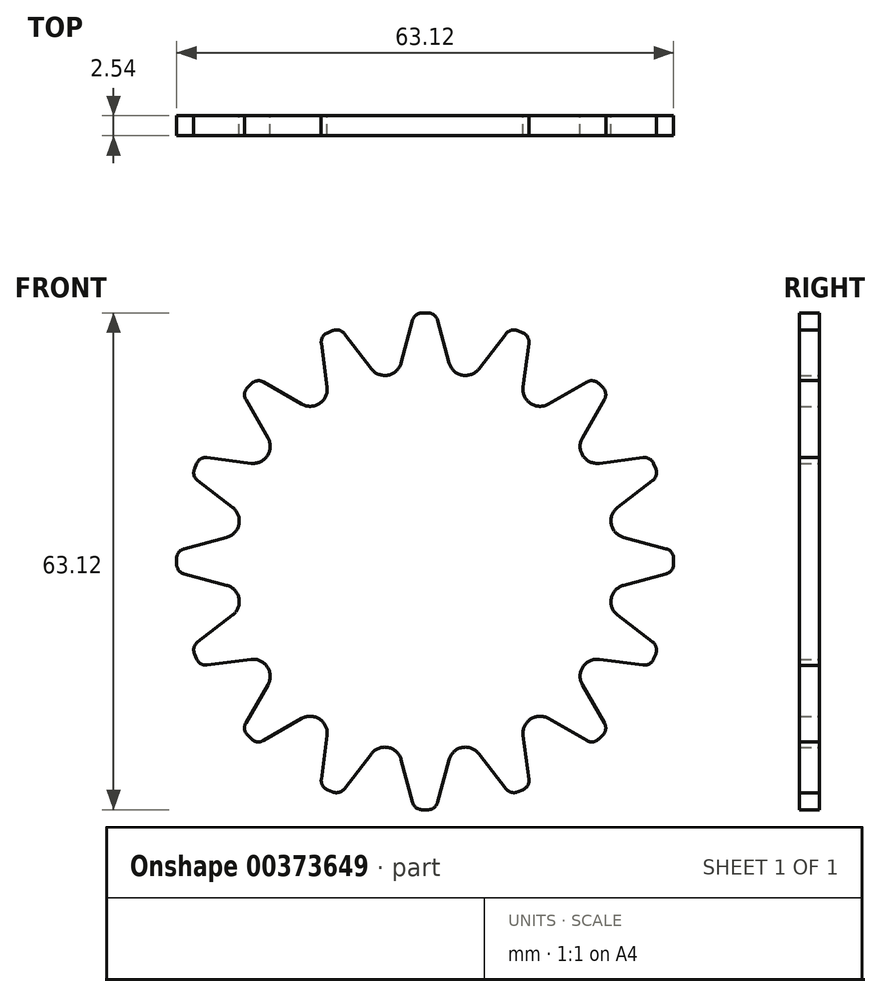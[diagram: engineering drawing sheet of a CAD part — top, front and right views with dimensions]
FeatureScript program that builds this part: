
annotation { "Feature Type Name" : "Feature", "Feature Type Description" : "" }
export const myFeature = defineFeature(function(context is Context, id is Id, definition is map)
    precondition{}
    {
        {
            var Q0;
            Q0=qCreatedBy(makeId("Front.planeOp"),FACE);
            var sketch = newSketch(context, id + "F0", { "sketchPlane" : qUnion([Q0])});
            skLineSegment(sketch, "E0", {"start": v(0, -18.83) * mm, "end": v(0, 46.05) * mm, "construction": true});
            skLineSegment(sketch, "E1", {"start": v(-3.04, 25.21) * mm, "end": v(-1.59, 30.62) * mm});
            skLineSegment(sketch, "E2", {"start": v(-0.36, 31.56) * mm, "end": v(0, 31.56) * mm});
            skPoint(sketch, "E3.visualSharp", {"position": v(-1.34, 31.56) * mm});
            skArc(sketch, "E3.filletArc", {"start": v(-0.36, 31.56) * mm, "mid": v(-1.13, 31.3) * mm, "end": v(-1.59, 30.62) * mm});
            skLineSegment(sketch, "E4.MirrorCS", {"start": v(0.36, 31.56) * mm, "end": v(0, 31.56) * mm});
            skArc(sketch, "E5.MirrorCS", {"start": v(0.36, 31.56) * mm, "mid": v(1.13, 31.3) * mm, "end": v(1.59, 30.62) * mm});
            skPoint(sketch, "E6.MirrorP", {"position": v(1.34, 31.56) * mm});
            skLineSegment(sketch, "E7.MirrorCS", {"start": v(3.04, 25.21) * mm, "end": v(1.59, 30.62) * mm});
            skCircle(sketch, "E8", {"center": v(0, 0) * mm, "radius": 25.4 * mm, "construction": true});
            skLineSegment(sketch, "E9.1.0", {"start": v(-6.84, 24.46) * mm, "end": v(-10.25, 28.9) * mm});
            skArc(sketch, "E9.1.1", {"start": v(-11.75, 29.3) * mm, "mid": v(-10.93, 29.35) * mm, "end": v(-10.25, 28.9) * mm});
            skPoint(sketch, "E9.1.2", {"position": v(-10.85, 29.67) * mm});
            skLineSegment(sketch, "E9.1.3", {"start": v(-12.41, 29.02) * mm, "end": v(-12.08, 29.16) * mm});
            skLineSegment(sketch, "E9.1.4", {"start": v(-11.75, 29.3) * mm, "end": v(-12.08, 29.16) * mm});
            skArc(sketch, "E9.1.5", {"start": v(-12.41, 29.02) * mm, "mid": v(-13.03, 28.48) * mm, "end": v(-13.19, 27.68) * mm});
            skPoint(sketch, "E9.1.6", {"position": v(-13.31, 28.65) * mm});
            skLineSegment(sketch, "E9.1.7", {"start": v(-12.45, 22.13) * mm, "end": v(-13.19, 27.68) * mm});
            skLineSegment(sketch, "E9.2.0", {"start": v(-15.68, 19.98) * mm, "end": v(-20.53, 22.78) * mm});
            skArc(sketch, "E9.2.1", {"start": v(-22.06, 22.57) * mm, "mid": v(-21.33, 22.93) * mm, "end": v(-20.53, 22.78) * mm});
            skPoint(sketch, "E9.2.2", {"position": v(-21.37, 23.26) * mm});
            skLineSegment(sketch, "E9.2.3", {"start": v(-22.57, 22.06) * mm, "end": v(-22.32, 22.32) * mm});
            skLineSegment(sketch, "E9.2.4", {"start": v(-22.06, 22.57) * mm, "end": v(-22.32, 22.32) * mm});
            skArc(sketch, "E9.2.5", {"start": v(-22.57, 22.06) * mm, "mid": v(-22.93, 21.33) * mm, "end": v(-22.78, 20.53) * mm});
            skPoint(sketch, "E9.2.6", {"position": v(-23.26, 21.37) * mm});
            skLineSegment(sketch, "E9.2.7", {"start": v(-19.98, 15.68) * mm, "end": v(-22.78, 20.53) * mm});
            skLineSegment(sketch, "E9.3.0", {"start": v(-22.13, 12.45) * mm, "end": v(-27.68, 13.19) * mm});
            skArc(sketch, "E9.3.1", {"start": v(-29.02, 12.41) * mm, "mid": v(-28.48, 13.03) * mm, "end": v(-27.68, 13.19) * mm});
            skPoint(sketch, "E9.3.2", {"position": v(-28.65, 13.31) * mm});
            skLineSegment(sketch, "E9.3.3", {"start": v(-29.3, 11.75) * mm, "end": v(-29.16, 12.08) * mm});
            skLineSegment(sketch, "E9.3.4", {"start": v(-29.02, 12.41) * mm, "end": v(-29.16, 12.08) * mm});
            skArc(sketch, "E9.3.5", {"start": v(-29.3, 11.75) * mm, "mid": v(-29.35, 10.93) * mm, "end": v(-28.9, 10.25) * mm});
            skPoint(sketch, "E9.3.6", {"position": v(-29.67, 10.85) * mm});
            skLineSegment(sketch, "E9.3.7", {"start": v(-24.46, 6.84) * mm, "end": v(-28.9, 10.25) * mm});
            skLineSegment(sketch, "E9.4.0", {"start": v(-25.21, 3.04) * mm, "end": v(-30.62, 1.59) * mm});
            skArc(sketch, "E9.4.1", {"start": v(-31.56, 0.36) * mm, "mid": v(-31.3, 1.13) * mm, "end": v(-30.62, 1.59) * mm});
            skPoint(sketch, "E9.4.2", {"position": v(-31.56, 1.34) * mm});
            skLineSegment(sketch, "E9.4.3", {"start": v(-31.56, -0.36) * mm, "end": v(-31.56, 0) * mm});
            skLineSegment(sketch, "E9.4.4", {"start": v(-31.56, 0.36) * mm, "end": v(-31.56, 0) * mm});
            skArc(sketch, "E9.4.5", {"start": v(-31.56, -0.36) * mm, "mid": v(-31.3, -1.13) * mm, "end": v(-30.62, -1.59) * mm});
            skPoint(sketch, "E9.4.6", {"position": v(-31.56, -1.34) * mm});
            skLineSegment(sketch, "E9.4.7", {"start": v(-25.21, -3.04) * mm, "end": v(-30.62, -1.59) * mm});
            skLineSegment(sketch, "E9.5.0", {"start": v(-24.46, -6.84) * mm, "end": v(-28.9, -10.25) * mm});
            skArc(sketch, "E9.5.1", {"start": v(-29.3, -11.75) * mm, "mid": v(-29.35, -10.93) * mm, "end": v(-28.9, -10.25) * mm});
            skPoint(sketch, "E9.5.2", {"position": v(-29.67, -10.85) * mm});
            skLineSegment(sketch, "E9.5.3", {"start": v(-29.02, -12.41) * mm, "end": v(-29.16, -12.08) * mm});
            skLineSegment(sketch, "E9.5.4", {"start": v(-29.3, -11.75) * mm, "end": v(-29.16, -12.08) * mm});
            skArc(sketch, "E9.5.5", {"start": v(-29.02, -12.41) * mm, "mid": v(-28.48, -13.03) * mm, "end": v(-27.68, -13.19) * mm});
            skPoint(sketch, "E9.5.6", {"position": v(-28.65, -13.31) * mm});
            skLineSegment(sketch, "E9.5.7", {"start": v(-22.13, -12.45) * mm, "end": v(-27.68, -13.19) * mm});
            skLineSegment(sketch, "E9.6.0", {"start": v(-19.98, -15.68) * mm, "end": v(-22.78, -20.53) * mm});
            skArc(sketch, "E9.6.1", {"start": v(-22.57, -22.06) * mm, "mid": v(-22.93, -21.33) * mm, "end": v(-22.78, -20.53) * mm});
            skPoint(sketch, "E9.6.2", {"position": v(-23.26, -21.37) * mm});
            skLineSegment(sketch, "E9.6.3", {"start": v(-22.06, -22.57) * mm, "end": v(-22.32, -22.32) * mm});
            skLineSegment(sketch, "E9.6.4", {"start": v(-22.57, -22.06) * mm, "end": v(-22.32, -22.32) * mm});
            skArc(sketch, "E9.6.5", {"start": v(-22.06, -22.57) * mm, "mid": v(-21.33, -22.93) * mm, "end": v(-20.53, -22.78) * mm});
            skPoint(sketch, "E9.6.6", {"position": v(-21.37, -23.26) * mm});
            skLineSegment(sketch, "E9.6.7", {"start": v(-15.68, -19.98) * mm, "end": v(-20.53, -22.78) * mm});
            skLineSegment(sketch, "E9.7.0", {"start": v(-12.45, -22.13) * mm, "end": v(-13.19, -27.68) * mm});
            skArc(sketch, "E9.7.1", {"start": v(-12.41, -29.02) * mm, "mid": v(-13.03, -28.48) * mm, "end": v(-13.19, -27.68) * mm});
            skPoint(sketch, "E9.7.2", {"position": v(-13.31, -28.65) * mm});
            skLineSegment(sketch, "E9.7.3", {"start": v(-11.75, -29.3) * mm, "end": v(-12.08, -29.16) * mm});
            skLineSegment(sketch, "E9.7.4", {"start": v(-12.41, -29.02) * mm, "end": v(-12.08, -29.16) * mm});
            skArc(sketch, "E9.7.5", {"start": v(-11.75, -29.3) * mm, "mid": v(-10.93, -29.35) * mm, "end": v(-10.25, -28.9) * mm});
            skPoint(sketch, "E9.7.6", {"position": v(-10.85, -29.67) * mm});
            skLineSegment(sketch, "E9.7.7", {"start": v(-6.84, -24.46) * mm, "end": v(-10.25, -28.9) * mm});
            skLineSegment(sketch, "E9.8.0", {"start": v(-3.04, -25.21) * mm, "end": v(-1.59, -30.62) * mm});
            skArc(sketch, "E9.8.1", {"start": v(-0.36, -31.56) * mm, "mid": v(-1.13, -31.3) * mm, "end": v(-1.59, -30.62) * mm});
            skPoint(sketch, "E9.8.2", {"position": v(-1.34, -31.56) * mm});
            skLineSegment(sketch, "E9.8.3", {"start": v(0.36, -31.56) * mm, "end": v(0, -31.56) * mm});
            skLineSegment(sketch, "E9.8.4", {"start": v(-0.36, -31.56) * mm, "end": v(0, -31.56) * mm});
            skArc(sketch, "E9.8.5", {"start": v(0.36, -31.56) * mm, "mid": v(1.13, -31.3) * mm, "end": v(1.59, -30.62) * mm});
            skPoint(sketch, "E9.8.6", {"position": v(1.34, -31.56) * mm});
            skLineSegment(sketch, "E9.8.7", {"start": v(3.04, -25.21) * mm, "end": v(1.59, -30.62) * mm});
            skLineSegment(sketch, "E9.9.0", {"start": v(6.84, -24.46) * mm, "end": v(10.25, -28.9) * mm});
            skArc(sketch, "E9.9.1", {"start": v(11.75, -29.3) * mm, "mid": v(10.93, -29.35) * mm, "end": v(10.25, -28.9) * mm});
            skPoint(sketch, "E9.9.2", {"position": v(10.85, -29.67) * mm});
            skLineSegment(sketch, "E9.9.3", {"start": v(12.41, -29.02) * mm, "end": v(12.08, -29.16) * mm});
            skLineSegment(sketch, "E9.9.4", {"start": v(11.75, -29.3) * mm, "end": v(12.08, -29.16) * mm});
            skArc(sketch, "E9.9.5", {"start": v(12.41, -29.02) * mm, "mid": v(13.03, -28.48) * mm, "end": v(13.19, -27.68) * mm});
            skPoint(sketch, "E9.9.6", {"position": v(13.31, -28.65) * mm});
            skLineSegment(sketch, "E9.9.7", {"start": v(12.45, -22.13) * mm, "end": v(13.19, -27.68) * mm});
            skLineSegment(sketch, "E9.10.0", {"start": v(15.68, -19.98) * mm, "end": v(20.53, -22.78) * mm});
            skArc(sketch, "E9.10.1", {"start": v(22.06, -22.57) * mm, "mid": v(21.33, -22.93) * mm, "end": v(20.53, -22.78) * mm});
            skPoint(sketch, "E9.10.2", {"position": v(21.37, -23.26) * mm});
            skLineSegment(sketch, "E9.10.3", {"start": v(22.57, -22.06) * mm, "end": v(22.32, -22.32) * mm});
            skLineSegment(sketch, "E9.10.4", {"start": v(22.06, -22.57) * mm, "end": v(22.32, -22.32) * mm});
            skArc(sketch, "E9.10.5", {"start": v(22.57, -22.06) * mm, "mid": v(22.93, -21.33) * mm, "end": v(22.78, -20.53) * mm});
            skPoint(sketch, "E9.10.6", {"position": v(23.26, -21.37) * mm});
            skLineSegment(sketch, "E9.10.7", {"start": v(19.98, -15.68) * mm, "end": v(22.78, -20.53) * mm});
            skLineSegment(sketch, "E9.11.0", {"start": v(22.13, -12.45) * mm, "end": v(27.68, -13.19) * mm});
            skArc(sketch, "E9.11.1", {"start": v(29.02, -12.41) * mm, "mid": v(28.48, -13.03) * mm, "end": v(27.68, -13.19) * mm});
            skPoint(sketch, "E9.11.2", {"position": v(28.65, -13.31) * mm});
            skLineSegment(sketch, "E9.11.3", {"start": v(29.3, -11.75) * mm, "end": v(29.16, -12.08) * mm});
            skLineSegment(sketch, "E9.11.4", {"start": v(29.02, -12.41) * mm, "end": v(29.16, -12.08) * mm});
            skArc(sketch, "E9.11.5", {"start": v(29.3, -11.75) * mm, "mid": v(29.35, -10.93) * mm, "end": v(28.9, -10.25) * mm});
            skPoint(sketch, "E9.11.6", {"position": v(29.67, -10.85) * mm});
            skLineSegment(sketch, "E9.11.7", {"start": v(24.46, -6.84) * mm, "end": v(28.9, -10.25) * mm});
            skLineSegment(sketch, "E9.12.0", {"start": v(25.21, -3.04) * mm, "end": v(30.62, -1.59) * mm});
            skArc(sketch, "E9.12.1", {"start": v(31.56, -0.36) * mm, "mid": v(31.3, -1.13) * mm, "end": v(30.62, -1.59) * mm});
            skPoint(sketch, "E9.12.2", {"position": v(31.56, -1.34) * mm});
            skLineSegment(sketch, "E9.12.3", {"start": v(31.56, 0.36) * mm, "end": v(31.56, 0) * mm});
            skLineSegment(sketch, "E9.12.4", {"start": v(31.56, -0.36) * mm, "end": v(31.56, 0) * mm});
            skArc(sketch, "E9.12.5", {"start": v(31.56, 0.36) * mm, "mid": v(31.3, 1.13) * mm, "end": v(30.62, 1.59) * mm});
            skPoint(sketch, "E9.12.6", {"position": v(31.56, 1.34) * mm});
            skLineSegment(sketch, "E9.12.7", {"start": v(25.21, 3.04) * mm, "end": v(30.62, 1.59) * mm});
            skLineSegment(sketch, "E9.13.0", {"start": v(24.46, 6.84) * mm, "end": v(28.9, 10.25) * mm});
            skArc(sketch, "E9.13.1", {"start": v(29.3, 11.75) * mm, "mid": v(29.35, 10.93) * mm, "end": v(28.9, 10.25) * mm});
            skPoint(sketch, "E9.13.2", {"position": v(29.67, 10.85) * mm});
            skLineSegment(sketch, "E9.13.3", {"start": v(29.02, 12.41) * mm, "end": v(29.16, 12.08) * mm});
            skLineSegment(sketch, "E9.13.4", {"start": v(29.3, 11.75) * mm, "end": v(29.16, 12.08) * mm});
            skArc(sketch, "E9.13.5", {"start": v(29.02, 12.41) * mm, "mid": v(28.48, 13.03) * mm, "end": v(27.68, 13.19) * mm});
            skPoint(sketch, "E9.13.6", {"position": v(28.65, 13.31) * mm});
            skLineSegment(sketch, "E9.13.7", {"start": v(22.13, 12.45) * mm, "end": v(27.68, 13.19) * mm});
            skLineSegment(sketch, "E9.14.0", {"start": v(19.98, 15.68) * mm, "end": v(22.78, 20.53) * mm});
            skArc(sketch, "E9.14.1", {"start": v(22.57, 22.06) * mm, "mid": v(22.93, 21.33) * mm, "end": v(22.78, 20.53) * mm});
            skPoint(sketch, "E9.14.2", {"position": v(23.26, 21.37) * mm});
            skLineSegment(sketch, "E9.14.3", {"start": v(22.06, 22.57) * mm, "end": v(22.32, 22.32) * mm});
            skLineSegment(sketch, "E9.14.4", {"start": v(22.57, 22.06) * mm, "end": v(22.32, 22.32) * mm});
            skArc(sketch, "E9.14.5", {"start": v(22.06, 22.57) * mm, "mid": v(21.33, 22.93) * mm, "end": v(20.53, 22.78) * mm});
            skPoint(sketch, "E9.14.6", {"position": v(21.37, 23.26) * mm});
            skLineSegment(sketch, "E9.14.7", {"start": v(15.68, 19.98) * mm, "end": v(20.53, 22.78) * mm});
            skLineSegment(sketch, "E9.15.0", {"start": v(12.45, 22.13) * mm, "end": v(13.19, 27.68) * mm});
            skArc(sketch, "E9.15.1", {"start": v(12.41, 29.02) * mm, "mid": v(13.03, 28.48) * mm, "end": v(13.19, 27.68) * mm});
            skPoint(sketch, "E9.15.2", {"position": v(13.31, 28.65) * mm});
            skLineSegment(sketch, "E9.15.3", {"start": v(11.75, 29.3) * mm, "end": v(12.08, 29.16) * mm});
            skLineSegment(sketch, "E9.15.4", {"start": v(12.41, 29.02) * mm, "end": v(12.08, 29.16) * mm});
            skArc(sketch, "E9.15.5", {"start": v(11.75, 29.3) * mm, "mid": v(10.93, 29.35) * mm, "end": v(10.25, 28.9) * mm});
            skPoint(sketch, "E9.15.6", {"position": v(10.85, 29.67) * mm});
            skLineSegment(sketch, "E9.15.7", {"start": v(6.84, 24.46) * mm, "end": v(10.25, 28.9) * mm});
            skArc(sketch, "E10", {"start": v(-15.68, 19.98) * mm, "mid": v(-13.4, 20.05) * mm, "end": v(-12.45, 22.13) * mm});
            skArc(sketch, "E11", {"start": v(-6.84, 24.46) * mm, "mid": v(-4.7, 23.65) * mm, "end": v(-3.04, 25.21) * mm});
            skArc(sketch, "E12", {"start": v(3.04, 25.21) * mm, "mid": v(4.7, 23.65) * mm, "end": v(6.84, 24.46) * mm});
            skArc(sketch, "E13", {"start": v(12.45, 22.13) * mm, "mid": v(13.4, 20.05) * mm, "end": v(15.68, 19.98) * mm});
            skArc(sketch, "E14", {"start": v(19.98, 15.68) * mm, "mid": v(20.05, 13.4) * mm, "end": v(22.13, 12.45) * mm});
            skArc(sketch, "E15", {"start": v(24.46, 6.84) * mm, "mid": v(23.65, 4.7) * mm, "end": v(25.21, 3.04) * mm});
            skArc(sketch, "E16", {"start": v(25.21, -3.04) * mm, "mid": v(23.65, -4.7) * mm, "end": v(24.46, -6.84) * mm});
            skArc(sketch, "E17", {"start": v(22.13, -12.45) * mm, "mid": v(20.05, -13.4) * mm, "end": v(19.98, -15.68) * mm});
            skArc(sketch, "E18", {"start": v(15.68, -19.98) * mm, "mid": v(13.4, -20.05) * mm, "end": v(12.45, -22.13) * mm});
            skArc(sketch, "E19", {"start": v(6.84, -24.46) * mm, "mid": v(4.7, -23.65) * mm, "end": v(3.04, -25.21) * mm});
            skArc(sketch, "E20", {"start": v(-3.04, -25.21) * mm, "mid": v(-4.7, -23.65) * mm, "end": v(-6.84, -24.46) * mm});
            skArc(sketch, "E21", {"start": v(-12.45, -22.13) * mm, "mid": v(-13.4, -20.05) * mm, "end": v(-15.68, -19.98) * mm});
            skArc(sketch, "E22", {"start": v(-19.98, -15.68) * mm, "mid": v(-20.05, -13.4) * mm, "end": v(-22.13, -12.45) * mm});
            skArc(sketch, "E23", {"start": v(-24.46, -6.84) * mm, "mid": v(-23.65, -4.7) * mm, "end": v(-25.21, -3.04) * mm});
            skArc(sketch, "E24", {"start": v(-25.21, 3.04) * mm, "mid": v(-23.65, 4.7) * mm, "end": v(-24.46, 6.84) * mm});
            skArc(sketch, "E25", {"start": v(-22.13, 12.45) * mm, "mid": v(-20.05, 13.4) * mm, "end": v(-19.98, 15.68) * mm});
            skSolve(sketch);
        }
        {
            var Q0;
            Q0 = qSketchRegion(id + "F0", true);
            extrude(context, id + "F1", {"entities" : qUnion([Q0]), "depth" : 2.54 * mm});
        }
    });
